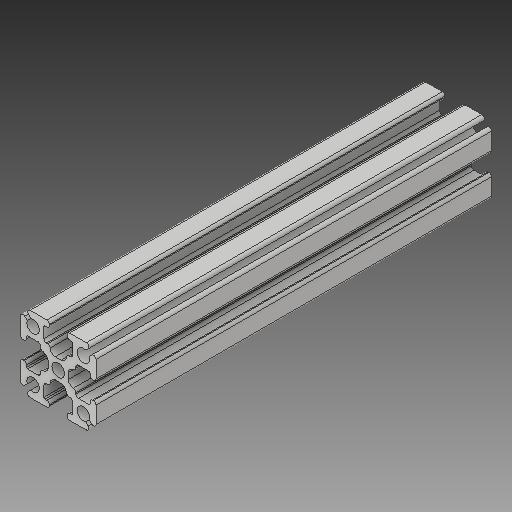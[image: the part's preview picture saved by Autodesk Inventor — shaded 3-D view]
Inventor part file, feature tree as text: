
AUTODESK INVENTOR PART (.ipt)
format: ipt  version: 2018.3 (Build 223284000, 284)  size: 475,648 bytes
history: native  units: mm
features: sketch x5, other x3, extrude x1, plane x1, projected_geometry x1
ambient origin geometry x8: Origin, YZ Plane, XZ Plane, XY Plane, X Axis, Y Axis, Z Axis, Center Point
bodies: Solid1 (feature_tree)
feature tree (11):
  other  "2 inch rev.ipt"
  extrude  "Extrusion1"  Depth=10.0mm TaperAngle=0.0deg
  other  "Solid1::2 inch rev.ipt"
  other  "TaggingFeature1"
  sketch  "Sketch1"  dims[d0=10.0mm d1=10.0mm d2=0.0mm]
  sketch  "Sketch2"
  sketch  "Sketch3"
  sketch  "Sketch4"
  plane  "Work Plane1"
  sketch  "Sketch5"
  projected_geometry  "Projected Loop1"
